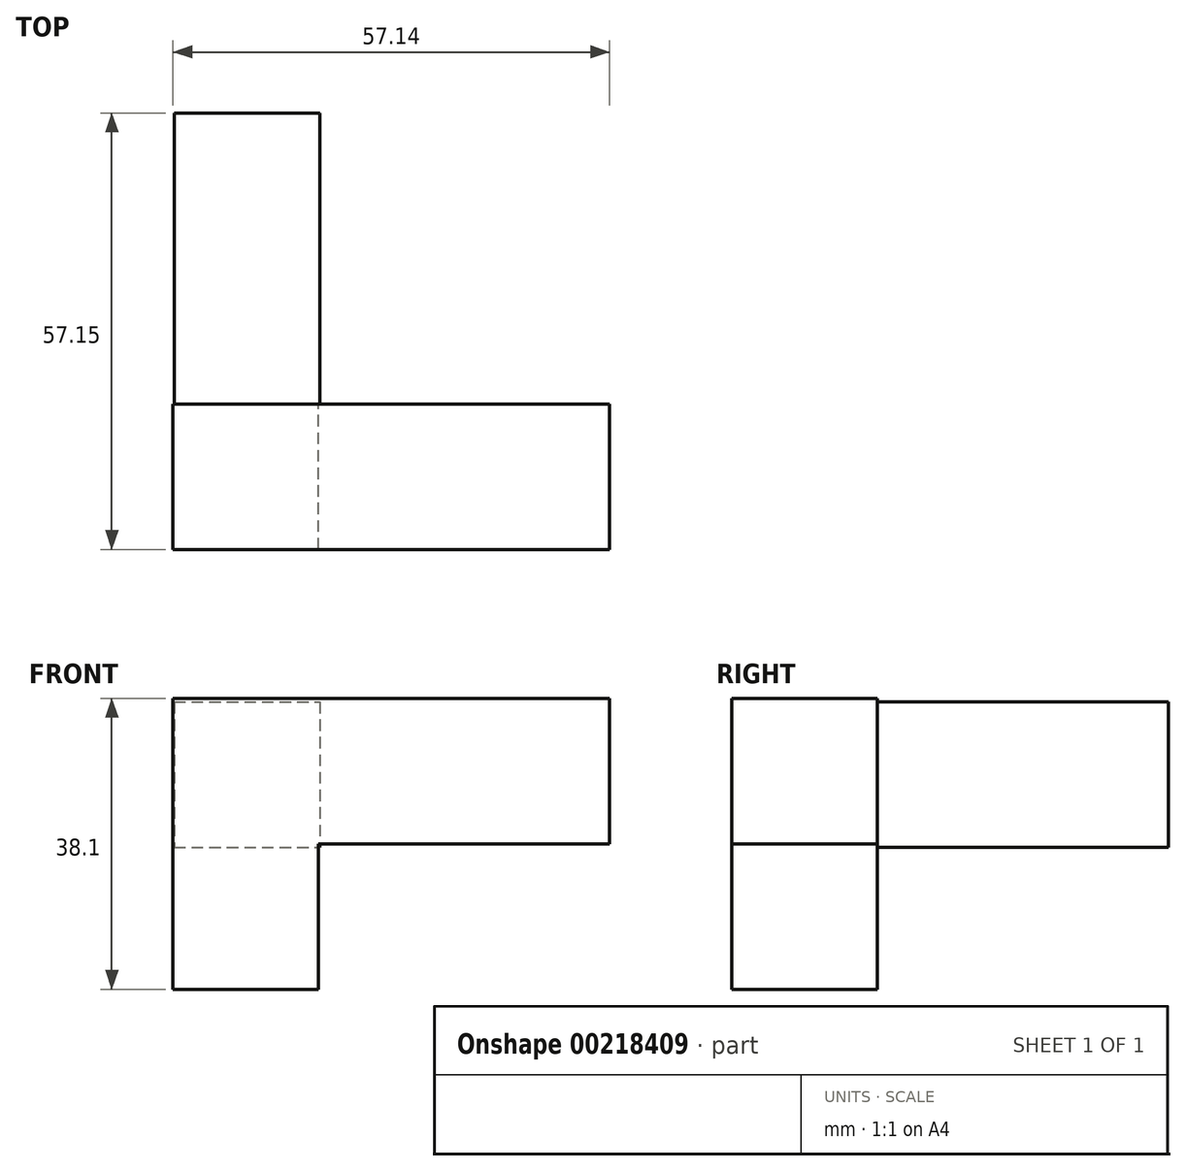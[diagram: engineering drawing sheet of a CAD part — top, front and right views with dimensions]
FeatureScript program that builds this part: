
annotation { "Feature Type Name" : "Feature", "Feature Type Description" : "" }
export const myFeature = defineFeature(function(context is Context, id is Id, definition is map)
    precondition{}
    {
        {
            var Q0;
            Q0=qCreatedBy(makeId("Front.planeOp"),FACE);
            var sketch = newSketch(context, id + "F0", { "sketchPlane" : qUnion([Q0])});
            skLineSegment(sketch, "E0.bottom", {"start": v(9.52, 9.53) * mm, "end": v(-9.52, 9.53) * mm});
            skLineSegment(sketch, "E0.top", {"start": v(9.53, -9.52) * mm, "end": v(-9.53, -9.52) * mm});
            skLineSegment(sketch, "E0.left", {"start": v(9.52, 9.53) * mm, "end": v(9.53, -9.52) * mm});
            skLineSegment(sketch, "E0.right", {"start": v(-9.53, 9.52) * mm, "end": v(-9.53, -9.52) * mm});
            skPoint(sketch, "E0.middle", {"position": v(0, 0) * mm});
            skLineSegment(sketch, "E1", {"start": v(9.52, 9.53) * mm, "end": v(28.57, 9.53) * mm});
            skLineSegment(sketch, "E2", {"start": v(28.57, 9.53) * mm, "end": v(28.57, -9.52) * mm});
            skLineSegment(sketch, "E3", {"start": v(28.57, -9.52) * mm, "end": v(9.53, -9.52) * mm});
            skLineSegment(sketch, "E4", {"start": v(-9.53, -9.52) * mm, "end": v(-28.58, -9.52) * mm});
            skLineSegment(sketch, "E5", {"start": v(-28.57, -9.52) * mm, "end": v(-28.58, 9.52) * mm});
            skLineSegment(sketch, "E6", {"start": v(-28.58, 9.52) * mm, "end": v(-9.52, 9.53) * mm});
            skLineSegment(sketch, "E7", {"start": v(-28.58, -9.52) * mm, "end": v(-28.57, -28.57) * mm});
            skLineSegment(sketch, "E8", {"start": v(-28.57, -28.57) * mm, "end": v(-9.52, -28.57) * mm});
            skLineSegment(sketch, "E9", {"start": v(-9.52, -28.57) * mm, "end": v(-9.53, -9.52) * mm});
            skLineSegment(sketch, "E10.bottom", {"start": v(-28.58, 9.52) * mm, "end": v(-9.53, 9.52) * mm});
            skLineSegment(sketch, "E10.top", {"start": v(-28.58, -9.52) * mm, "end": v(-9.53, -9.52) * mm});
            skLineSegment(sketch, "E10.left", {"start": v(-28.58, 9.52) * mm, "end": v(-28.58, -9.52) * mm});
            skSolve(sketch);
        }
        {
            var Q0;
            Q0 = qSketchRegion(id + "F0", true);
            extrude(context, id + "F1", {"entities" : qUnion([Q0]), "depth" : 19.05 * mm});
        }
        {
            var Q0;
            Q0=qCreatedBy(makeId("Front.planeOp"),FACE);
            var sketch = newSketch(context, id + "F2", { "sketchPlane" : qUnion([Q0])});
            skLineSegment(sketch, "E11.bottom", {"start": v(-28.42, 9.06) * mm, "end": v(-9.37, 9.06) * mm});
            skLineSegment(sketch, "E11.top", {"start": v(-28.42, -9.99) * mm, "end": v(-9.37, -9.99) * mm});
            skLineSegment(sketch, "E11.left", {"start": v(-28.42, 9.06) * mm, "end": v(-28.42, -9.99) * mm});
            skLineSegment(sketch, "E11.right", {"start": v(-9.37, 9.06) * mm, "end": v(-9.37, -9.99) * mm});
            skSolve(sketch);
        }
        {
            var Q0;
            Q0 = qSketchRegion(id + "F2", true);
            extrude(context, id + "F3", {"entities" : qUnion([Q0]), "operationType" : NewBodyOperationType.ADD, "oppositeDirection" : true, "depth" : 38.1 * mm});
        }
    });
